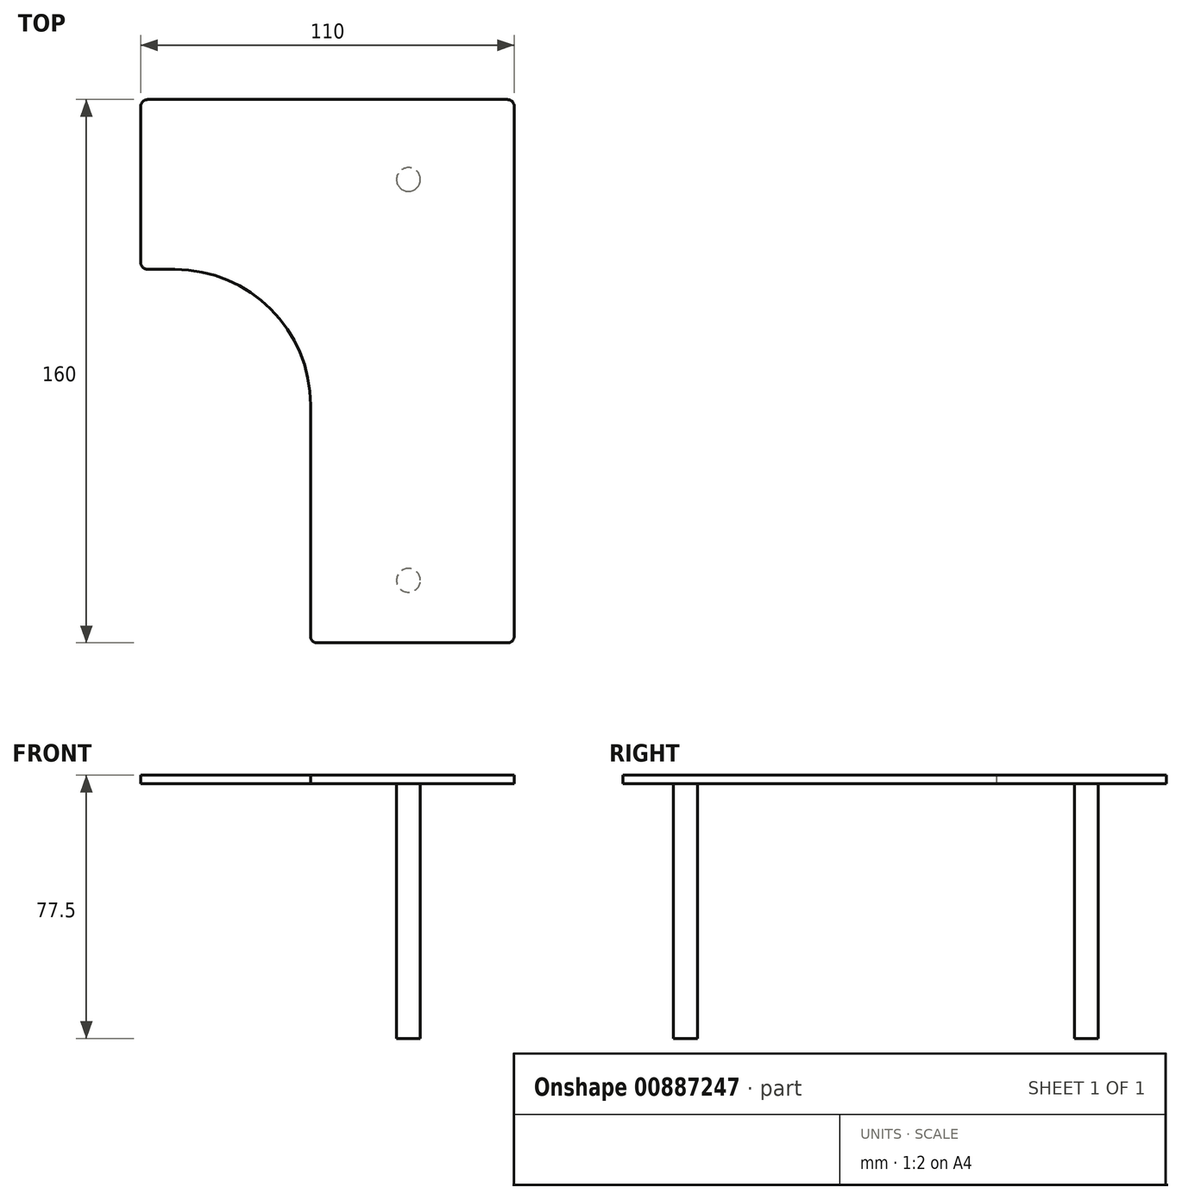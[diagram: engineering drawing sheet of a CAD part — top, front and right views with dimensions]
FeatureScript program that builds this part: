
annotation { "Feature Type Name" : "Feature", "Feature Type Description" : "" }
export const myFeature = defineFeature(function(context is Context, id is Id, definition is map)
    precondition{}
    {
        {
            var Q0;
            Q0=qCreatedBy(makeId("Top.planeOp"),FACE);
            var sketch = newSketch(context, id + "F0", { "sketchPlane" : qUnion([Q0])});
            skLineSegment(sketch, "E0", {"start": v(-2, 0) * mm, "end": v(-108, 0) * mm});
            skLineSegment(sketch, "E1", {"start": v(-110, -2) * mm, "end": v(-110, -158) * mm});
            skLineSegment(sketch, "E2", {"start": v(-108, -160) * mm, "end": v(-52, -160) * mm});
            skLineSegment(sketch, "E3", {"start": v(0, -2) * mm, "end": v(0, -48) * mm});
            skLineSegment(sketch, "E4", {"start": v(-2, -50) * mm, "end": v(-10, -50) * mm});
            skLineSegment(sketch, "E5", {"start": v(-50, -90) * mm, "end": v(-50, -158) * mm});
            skPoint(sketch, "E6.visualSharp", {"position": v(-50, -50) * mm});
            skArc(sketch, "E6.filletArc", {"start": v(-10, -50) * mm, "mid": v(-38.28, -61.72) * mm, "end": v(-50, -90) * mm});
            skPoint(sketch, "E7.visualSharp", {"position": v(-110, 0) * mm});
            skArc(sketch, "E7.filletArc", {"start": v(-108, 0) * mm, "mid": v(-109.41, -0.59) * mm, "end": v(-110, -2) * mm});
            skPoint(sketch, "E8.visualSharp", {"position": v(0, 0) * mm});
            skArc(sketch, "E8.filletArc", {"start": v(0, -2) * mm, "mid": v(-0.59, -0.59) * mm, "end": v(-2, 0) * mm});
            skPoint(sketch, "E9.visualSharp", {"position": v(-50, -160) * mm});
            skArc(sketch, "E9.filletArc", {"start": v(-52, -160) * mm, "mid": v(-50.59, -159.41) * mm, "end": v(-50, -158) * mm});
            skPoint(sketch, "E10.visualSharp", {"position": v(-110, -160) * mm});
            skArc(sketch, "E10.filletArc", {"start": v(-110, -158) * mm, "mid": v(-109.41, -159.41) * mm, "end": v(-108, -160) * mm});
            skPoint(sketch, "E11.visualSharp", {"position": v(0, -50) * mm});
            skArc(sketch, "E11.filletArc", {"start": v(-2, -50) * mm, "mid": v(-0.59, -49.41) * mm, "end": v(0, -48) * mm});
            skSolve(sketch);
        }
        {
            var Q0;
            Q0=makeQuery(id+"F0.imprint","IMPRINT",FACE,{"disambiguationData":[TD([[makeQuery(id+"F0.imprint","IMPRINT",EDGE,{"derivedFrom":sQuery(id+"F0.wireOp",EDGE,"E0")}),1.0]])]});
            extrude(context, id + "F1", {"entities" : qUnion([Q0]), "depth" : 2.5 * mm, "offsetDistance" : 25 * mm});
        }
        {
            var Q0;
            Q0=makeQuery(id+"F1.opExtrude","CAP_FACE",FACE,{"disambiguationData":[OSD([sQuery(id+"F0.wireOp",EDGE,"E0"),sQuery(id+"F0.wireOp",EDGE,"E1"),sQuery(id+"F0.wireOp",EDGE,"E2"),sQuery(id+"F0.wireOp",EDGE,"E3"),sQuery(id+"F0.wireOp",EDGE,"E4"),sQuery(id+"F0.wireOp",EDGE,"E5"),sQuery(id+"F0.wireOp",EDGE,"E6.filletArc"),sQuery(id+"F0.wireOp",EDGE,"E7.filletArc"),sQuery(id+"F0.wireOp",EDGE,"E8.filletArc"),sQuery(id+"F0.wireOp",EDGE,"E9.filletArc"),sQuery(id+"F0.wireOp",EDGE,"E10.filletArc"),sQuery(id+"F0.wireOp",EDGE,"E11.filletArc")])],"isStart":true});
            var sketch = newSketch(context, id + "F2", { "sketchPlane" : qUnion([Q0])});
            skCircle(sketch, "E12", {"center": v(-78.84, 141.6) * mm, "radius": 3.5 * mm});
            skCircle(sketch, "E13", {"center": v(-78.84, 23.55) * mm, "radius": 3.5 * mm});
            skSolve(sketch);
        }
        {
            var Q0;
            Q0=makeQuery(id+"F2.imprint","IMPRINT",FACE,{"disambiguationData":[TD([[makeQuery(id+"F2.imprint","IMPRINT",EDGE,{"derivedFrom":sQuery(id+"F2.wireOp",EDGE,"E12")}),1.0]])]});
            var Q1;
            Q1=makeQuery(id+"F2.imprint","IMPRINT",FACE,{"disambiguationData":[TD([[makeQuery(id+"F2.imprint","IMPRINT",EDGE,{"derivedFrom":sQuery(id+"F2.wireOp",EDGE,"E13")}),1.0]])]});
            extrude(context, id + "F3", {"entities" : qUnion([Q0, Q1]), "operationType" : NewBodyOperationType.ADD, "depth" : 75 * mm, "offsetDistance" : 25 * mm});
        }
        {
            var Q0;
            Q0=makeQuery(id+"F3.opExtrude","CAP_FACE",FACE,{"disambiguationData":[OSD([sQuery(id+"F2.wireOp",EDGE,"E12")])],"isStart":false});
            var sketch = newSketch(context, id + "F4", { "sketchPlane" : qUnion([Q0])});
            skCircle(sketch, "E14.0.0", {"center": v(-78.84, 141.6) * mm, "radius": 3.5 * mm});
            skLineSegment(sketch, "E15", {"start": v(-56.53, 141.6) * mm, "end": v(-104.53, 141.6) * mm});
            skArc(sketch, "E16.0.startCap", {"start": v(-56.53, 145.6) * mm, "mid": v(-52.53, 141.6) * mm, "end": v(-56.53, 137.6) * mm});
            skArc(sketch, "E16.0.endCap", {"start": v(-104.53, 137.6) * mm, "mid": v(-108.53, 141.6) * mm, "end": v(-104.53, 145.6) * mm});
            skLineSegment(sketch, "E16.0.left", {"start": v(-56.53, 137.6) * mm, "end": v(-104.53, 137.6) * mm});
            skLineSegment(sketch, "E16.0.right", {"start": v(-56.53, 145.6) * mm, "end": v(-104.53, 145.6) * mm});
            skCircle(sketch, "E17.0", {"center": v(-78.84, 23.55) * mm, "radius": 3.5 * mm});
            skLineSegment(sketch, "E18", {"start": v(-104.53, 23.55) * mm, "end": v(-15.07, 23.55) * mm});
            skArc(sketch, "E19.0.startCap", {"start": v(-104.53, 19.55) * mm, "mid": v(-108.53, 23.55) * mm, "end": v(-104.53, 27.55) * mm});
            skArc(sketch, "E19.0.endCap", {"start": v(-15.07, 27.55) * mm, "mid": v(-11.07, 23.55) * mm, "end": v(-15.07, 19.55) * mm});
            skLineSegment(sketch, "E19.0.left", {"start": v(-104.53, 27.55) * mm, "end": v(-15.07, 27.55) * mm});
            skLineSegment(sketch, "E19.0.right", {"start": v(-104.53, 19.55) * mm, "end": v(-15.07, 19.55) * mm});
            skSolve(sketch);
        }
        {
            var Q0;
            Q0=makeQuery(id+"F4.imprint","IMPRINT",FACE,{"disambiguationData":[TD([[makeQuery(id+"F4.imprint","IMPRINT",EDGE,{"derivedFrom":sQuery(id+"F4.wireOp",EDGE,"E16.0.startCap")}),-1.0]])]});
            var Q1;
            Q1=makeQuery(id+"F4.imprint","IMPRINT",FACE,{"disambiguationData":[TD([[makeQuery(id+"F4.imprint","IMPRINT",EDGE,{"derivedFrom":sQuery(id+"F4.wireOp",EDGE,"E19.0.startCap")}),-1.0]])]});
            var Q2;
            {var subQ0=sQuery(id+"F4.wireOp",EDGE,"E18");var subQ1=sQuery(id+"F4.wireOp",EDGE,"E17.0");var subQ2=makeQuery(id+"F4.imprint","INTERSECT",VERTEX,{"disambiguationData":[OD(0.0)],"derivedFrom":[subQ1,subQ0]});Q2=makeQuery(id+"F4.imprint","IMPRINT",FACE,{"disambiguationData":[TD([[makeQuery(id+"F4.imprint","IMPRINT",EDGE,{"disambiguationData":[TD([[subQ2,1.0]])],"derivedFrom":subQ1}),1.0]])]});}
            extrude(context, id + "F5", {"entities" : qUnion([Q0, Q1, Q2]), "operationType" : NewBodyOperationType.ADD, "oppositeDirection" : true, "depth" : 2 * mm, "offsetDistance" : 25 * mm});
        }
        {
            var Q0;
            Q0=makeQuery(id+"F1.opExtrude","SWEPT_BODY",BODY,{"disambiguationData":[OSD([sQuery(id+"F0.wireOp",EDGE,"E0"),sQuery(id+"F0.wireOp",EDGE,"E1"),sQuery(id+"F0.wireOp",EDGE,"E2"),sQuery(id+"F0.wireOp",EDGE,"E3"),sQuery(id+"F0.wireOp",EDGE,"E4"),sQuery(id+"F0.wireOp",EDGE,"E5"),sQuery(id+"F0.wireOp",EDGE,"E6.filletArc"),sQuery(id+"F0.wireOp",EDGE,"E7.filletArc"),sQuery(id+"F0.wireOp",EDGE,"E8.filletArc"),sQuery(id+"F0.wireOp",EDGE,"E9.filletArc"),sQuery(id+"F0.wireOp",EDGE,"E10.filletArc"),sQuery(id+"F0.wireOp",EDGE,"E11.filletArc")])]});
            var Q1;
            Q1=qCreatedBy(makeId("Right.planeOp"),FACE);
            mirror(context, id + "F6", {"entities" : qUnion([Q0]), "mirrorPlane" : qUnion([Q1])});
        }
        {
            var Q0;
            Q0=makeQuery(id+"F1.opExtrude","SWEPT_BODY",BODY,{"disambiguationData":[OSD([sQuery(id+"F0.wireOp",EDGE,"E0"),sQuery(id+"F0.wireOp",EDGE,"E1"),sQuery(id+"F0.wireOp",EDGE,"E2"),sQuery(id+"F0.wireOp",EDGE,"E3"),sQuery(id+"F0.wireOp",EDGE,"E4"),sQuery(id+"F0.wireOp",EDGE,"E5"),sQuery(id+"F0.wireOp",EDGE,"E6.filletArc"),sQuery(id+"F0.wireOp",EDGE,"E7.filletArc"),sQuery(id+"F0.wireOp",EDGE,"E8.filletArc"),sQuery(id+"F0.wireOp",EDGE,"E9.filletArc"),sQuery(id+"F0.wireOp",EDGE,"E10.filletArc"),sQuery(id+"F0.wireOp",EDGE,"E11.filletArc")])]});
            deleteBodies(context, id + "F7", {"entities" : qUnion([Q0])});
        }
    });
